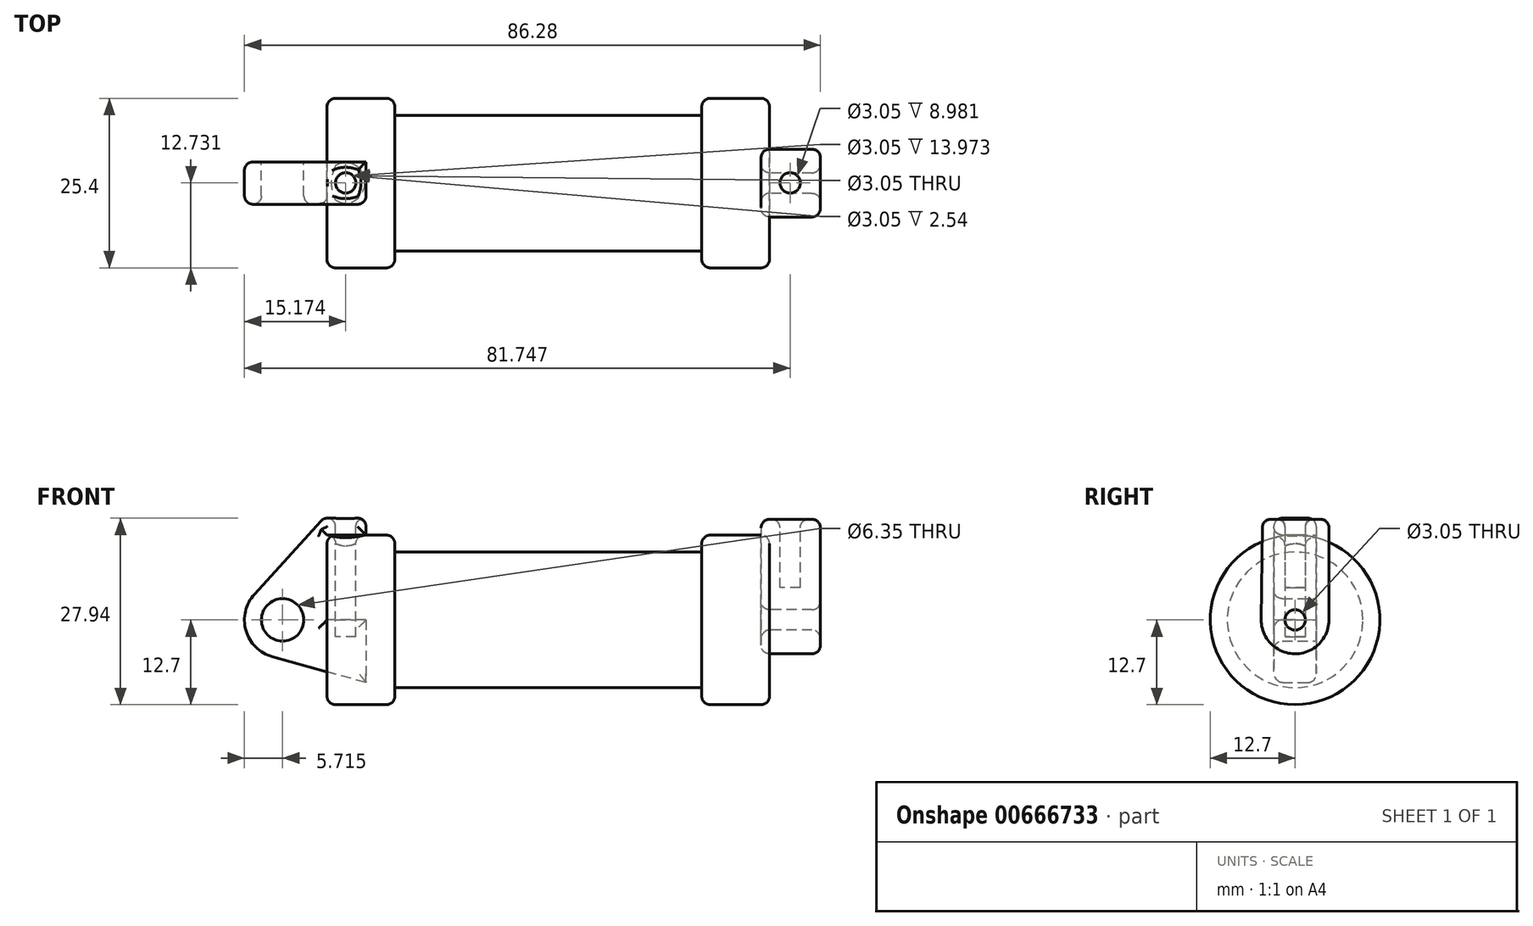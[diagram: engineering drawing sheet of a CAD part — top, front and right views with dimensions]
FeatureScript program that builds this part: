
annotation { "Feature Type Name" : "Feature", "Feature Type Description" : "" }
export const myFeature = defineFeature(function(context is Context, id is Id, definition is map)
    precondition{}
    {
        {
            var Q0;
            Q0=qCreatedBy(makeId("Front.planeOp"),FACE);
            var sketch = newSketch(context, id + "F0", { "sketchPlane" : qUnion([Q0])});
            skLineSegment(sketch, "E0", {"start": v(0, 0) * mm, "end": v(0, 12.7) * mm});
            skLineSegment(sketch, "E1", {"start": v(0, 12.7) * mm, "end": v(10.16, 12.7) * mm});
            skLineSegment(sketch, "E2", {"start": v(10.16, 12.7) * mm, "end": v(10.16, 10.16) * mm});
            skLineSegment(sketch, "E3", {"start": v(10.16, 10.16) * mm, "end": v(56.13, 10.16) * mm});
            skLineSegment(sketch, "E4", {"start": v(56.13, 10.16) * mm, "end": v(56.13, 12.7) * mm});
            skLineSegment(sketch, "E5", {"start": v(56.13, 12.7) * mm, "end": v(66.3, 12.7) * mm});
            skLineSegment(sketch, "E6", {"start": v(66.3, 12.7) * mm, "end": v(66.3, 0) * mm});
            skLineSegment(sketch, "E7", {"start": v(66.3, 0) * mm, "end": v(0, 0) * mm});
            skLineSegment(sketch, "E8", {"start": v(5.84, 15.24) * mm, "end": v(-0.5, 15.24) * mm});
            skLineSegment(sketch, "E9", {"start": v(-0.5, 15.24) * mm, "end": v(-10.88, 3.85) * mm});
            skLineSegment(sketch, "E10", {"start": v(0, 0) * mm, "end": v(-6.65, 0) * mm});
            skCircle(sketch, "E11", {"center": v(-6.65, 0) * mm, "radius": 5.72 * mm});
            skCircle(sketch, "E12", {"center": v(-6.65, 0) * mm, "radius": 3.18 * mm});
            skLineSegment(sketch, "E13", {"start": v(5.84, 15.24) * mm, "end": v(5.84, -9.4) * mm});
            skLineSegment(sketch, "E14", {"start": v(5.84, -9.4) * mm, "end": v(-8.18, -5.5) * mm});
            skSolve(sketch);
        }
        {
            var Q0;
            {var subQ1=sQuery(id+"F0.wireOp",EDGE,"E0");Q0=makeQuery(id+"F0.imprint","IMPRINT",FACE,{"disambiguationData":[TD([[makeQuery(id+"F0.imprint","IMPRINT",EDGE,{"derivedFrom":subQ1}),1.0]])]});}
            var Q1;
            {var subQ0=sQuery(id+"F0.wireOp",EDGE,"E14");Q1=makeQuery(id+"F0.imprint","IMPRINT",FACE,{"disambiguationData":[TD([[makeQuery(id+"F0.imprint","IMPRINT",EDGE,{"derivedFrom":subQ0}),-1.0]])]});}
            var Q2;
            {var subQ5=sQuery(id+"F0.wireOp",EDGE,"E12");Q2=makeQuery(id+"F0.imprint","IMPRINT",FACE,{"disambiguationData":[TD([[makeQuery(id+"F0.imprint","IMPRINT",EDGE,{"derivedFrom":subQ5}),-1.0]])]});}
            extrude(context, id + "F1", {"entities" : qUnion([Q0, Q1, Q2]), "endBound" : BoundingType.SYMMETRIC, "depth" : 6.35 * mm, "offsetDistance" : 25.4 * mm});
        }
        {
            var Q0;
            {var subQ0=sQuery(id+"F0.wireOp",EDGE,"E2");Q0=makeQuery(id+"F0.imprint","IMPRINT",FACE,{"disambiguationData":[TD([[makeQuery(id+"F0.imprint","IMPRINT",EDGE,{"derivedFrom":subQ0}),-1.0]])]});}
            var Q1;
            {var subQ0=sQuery(id+"F0.wireOp",EDGE,"E0");Q1=makeQuery(id+"F0.imprint","IMPRINT",FACE,{"disambiguationData":[TD([[makeQuery(id+"F0.imprint","IMPRINT",EDGE,{"derivedFrom":subQ0}),-1.0]])]});}
            var Q2;
            Q2=sQuery(id+"F0.wireOp",EDGE,"E7");
            revolve(context, id + "F2", {"entities" : qUnion([Q0, Q1]), "axis" : qUnion([Q2]), "revolveType" : RevolveType.FULL});
        }
        {
            var Q0;
            Q0=makeQuery(id+"F2.opRevolve","SWEPT_FACE",FACE,{"disambiguationData":[OSD([sQuery(id+"F0.wireOp",EDGE,"E6")])]});
            var sketch = newSketch(context, id + "F3", { "sketchPlane" : qUnion([Q0])});
            skCircle(sketch, "E15", {"center": v(0, 0) * mm, "radius": 1.52 * mm});
            skCircle(sketch, "E16", {"center": v(0, 0) * mm, "radius": 5.08 * mm});
            skLineSegment(sketch, "E17", {"start": v(5.08, 0) * mm, "end": v(5.08, 15.08) * mm});
            skLineSegment(sketch, "E18", {"start": v(5.08, 15.08) * mm, "end": v(-4.9, 15.08) * mm});
            skLineSegment(sketch, "E19", {"start": v(-4.9, 15.08) * mm, "end": v(-5.08, 0.03) * mm});
            skSolve(sketch);
        }
        {
            var Q0;
            Q0 = qSketchRegion(id + "F3", true);
            extrude(context, id + "F4", {"entities" : qUnion([Q0]), "depth" : 7.62 * mm, "offsetDistance" : 25.4 * mm, "hasSecondDirection" : true, "secondDirectionOppositeDirection" : true, "secondDirectionDepth" : 1.27 * mm});
        }
        {
            var Q0;
            Q0=makeQuery(id+"F2.opRevolve","SWEPT_FACE",FACE,{"disambiguationData":[OSD([sQuery(id+"F0.wireOp",EDGE,"E0")])]});
            var sketch = newSketch(context, id + "F5", { "sketchPlane" : qUnion([Q0])});
            skCircle(sketch, "E20", {"center": v(0, 0) * mm, "radius": 10.27 * mm});
            skSolve(sketch);
        }
        {
            var Q0;
            Q0=sQuery(id+"F5.wireOp",EDGE,"E20");
            extrude(context, id + "F6", {"bodyType" : ToolBodyType.SURFACE, "surfaceEntities" : qUnion([Q0]), "oppositeDirection" : true, "depth" : 63.5 * mm, "offsetDistance" : 25.4 * mm});
        }
        {
            var Q0;
            Q0=makeQuery(id+"F1.opExtrude","SWEPT_FACE",FACE,{"disambiguationData":[OSD([sQuery(id+"F0.wireOp",EDGE,"E8")])]});
            var sketch = newSketch(context, id + "F7", { "sketchPlane" : qUnion([Q0])});
            skCircle(sketch, "E21", {"center": v(2.8, 0.03) * mm, "radius": 1.52 * mm});
            skCircle(sketch, "E22", {"center": v(69.38, 0.03) * mm, "radius": 1.52 * mm});
            skSolve(sketch);
        }
        {
            var Q0;
            Q0=makeQuery(id+"F7.imprint","IMPRINT",FACE,{"disambiguationData":[TD([[makeQuery(id+"F7.imprint","IMPRINT",EDGE,{"derivedFrom":sQuery(id+"F7.wireOp",EDGE,"E21")}),1.0]])]});
            extrude(context, id + "F8", {"entities" : qUnion([Q0]), "operationType" : NewBodyOperationType.REMOVE, "oppositeDirection" : true, "depth" : 17.78 * mm, "offsetDistance" : 25.4 * mm});
        }
        {
            var Q0;
            Q0=makeQuery(id+"F7.imprint","IMPRINT",FACE,{"disambiguationData":[TD([[makeQuery(id+"F7.imprint","IMPRINT",EDGE,{"derivedFrom":sQuery(id+"F7.wireOp",EDGE,"E22")}),1.0]])]});
            extrude(context, id + "F9", {"entities" : qUnion([Q0]), "operationType" : NewBodyOperationType.REMOVE, "oppositeDirection" : true, "depth" : 10.4 * mm, "offsetDistance" : 25.4 * mm});
        }
        {
            var Q0;
            Q0=makeQuery(id+"F2.opRevolve","SWEPT_FACE",FACE,{"disambiguationData":[OSD([sQuery(id+"F0.wireOp",EDGE,"E1")])]});
            var Q1;
            Q1=makeQuery(id+"F6.opExtrude","SWEPT_FACE",FACE,{"disambiguationData":[OSD([sQuery(id+"F5.wireOp",EDGE,"E20")])]});
            var Q2;
            Q2=makeQuery(id+"F2.opRevolve","SWEPT_FACE",FACE,{"disambiguationData":[OSD([sQuery(id+"F0.wireOp",EDGE,"E5")])]});
            fillet(context, id + "F10", {"entities" : qUnion([Q0, Q1, Q2]), "radius" : 1.27 * mm, "tangentPropagation" : true, "allowEdgeOverflow" : false});
        }
        {
            var Q0;
            Q0=makeQuery(id+"F2.opRevolve","SWEPT_FACE",FACE,{"disambiguationData":[OSD([sQuery(id+"F0.wireOp",EDGE,"E6")])]});
            var Q1;
            Q1=makeQuery(id+"F1.opExtrude","SWEPT_FACE",FACE,{"disambiguationData":[OSD([sQuery(id+"F0.wireOp",EDGE,"E9")])]});
            var Q2;
            Q2=makeQuery(id+"F1.opExtrude","SWEPT_FACE",FACE,{"disambiguationData":[OSD([sQuery(id+"F0.wireOp",EDGE,"E8")])]});
            var Q3;
            Q3=makeQuery(id+"F1.opExtrude","SWEPT_FACE",FACE,{"disambiguationData":[OSD([sQuery(id+"F0.wireOp",EDGE,"E11")])]});
            var Q4;
            Q4=makeQuery(id+"F4.opExtrude","SWEPT_FACE",FACE,{"disambiguationData":[OSD([sQuery(id+"F3.wireOp",EDGE,"E18")])]});
            var Q5;
            Q5=makeQuery(id+"F9.opExtrude","CAP_EDGE",EDGE,{"disambiguationData":[OSD([sQuery(id+"F7.wireOp",EDGE,"E22")])],"isStart":false});
            var Q6;
            Q6=makeQuery(id+"F4.opExtrude","SWEPT_FACE",FACE,{"disambiguationData":[OSD([sQuery(id+"F3.wireOp",EDGE,"E17")])]});
            var Q7;
            Q7=makeQuery(id+"F4.opExtrude","SWEPT_FACE",FACE,{"disambiguationData":[OSD([sQuery(id+"F3.wireOp",EDGE,"E16")])]});
            var Q8;
            Q8=makeQuery(id+"F1.opExtrude","CAP_FACE",FACE,{"disambiguationData":[OSD([sQuery(id+"F0.wireOp",EDGE,"E0"),sQuery(id+"F0.wireOp",EDGE,"E1"),sQuery(id+"F0.wireOp",EDGE,"E7"),sQuery(id+"F0.wireOp",EDGE,"E8"),sQuery(id+"F0.wireOp",EDGE,"E9"),sQuery(id+"F0.wireOp",EDGE,"E11"),sQuery(id+"F0.wireOp",EDGE,"E12"),sQuery(id+"F0.wireOp",EDGE,"E13"),sQuery(id+"F0.wireOp",EDGE,"E14")])],"isStart":false});
            var Q9;
            Q9=makeQuery(id+"F8.opExtrude","CAP_EDGE",EDGE,{"disambiguationData":[OSD([sQuery(id+"F7.wireOp",EDGE,"E21")])],"isStart":true});
            var Q10;
            Q10=makeQuery(id+"F9.opExtrude","CAP_FACE",FACE,{"disambiguationData":[OSD([sQuery(id+"F7.wireOp",EDGE,"E22")])],"isStart":true});
            var Q11;
            Q11=makeQuery(id+"F4.opExtrude","CAP_EDGE",EDGE,{"disambiguationData":[OSD([sQuery(id+"F3.wireOp",EDGE,"E15")])],"isStart":false});
            var Q12;
            Q12=makeQuery(id+"F4.opExtrude","SWEPT_FACE",FACE,{"disambiguationData":[OSD([sQuery(id+"F3.wireOp",EDGE,"E19")])]});
            var Q13;
            Q13=makeQuery(id+"F4.opExtrude","CAP_EDGE",EDGE,{"disambiguationData":[OSD([sQuery(id+"F3.wireOp",EDGE,"E17")])],"isStart":false});
            var Q14;
            Q14=makeQuery(id+"F4.opExtrude","CAP_EDGE",EDGE,{"disambiguationData":[OSD([sQuery(id+"F3.wireOp",EDGE,"E16")])],"isStart":true});
            var Q15;
            Q15=makeQuery(id+"F4.opExtrude","SWEPT_EDGE",EDGE,{"disambiguationData":[OSD([sQuery(id+"F3.wireOp",EDGE,"E16"),sQuery(id+"F3.wireOp",EDGE,"E17")])]});
            var Q16;
            Q16=makeQuery(id+"F4.opExtrude","CAP_EDGE",EDGE,{"disambiguationData":[OSD([sQuery(id+"F3.wireOp",EDGE,"E19")])],"isStart":true});
            var Q17;
            Q17=makeQuery(id+"F4.opExtrude","SWEPT_EDGE",EDGE,{"disambiguationData":[OSD([sQuery(id+"F3.wireOp",EDGE,"E17"),sQuery(id+"F3.wireOp",EDGE,"E18")])]});
            var Q18;
            Q18=makeQuery(id+"F4.opExtrude","CAP_EDGE",EDGE,{"disambiguationData":[OSD([sQuery(id+"F3.wireOp",EDGE,"E17")])],"isStart":true});
            var Q19;
            Q19=makeQuery(id+"F4.opExtrude","CAP_EDGE",EDGE,{"disambiguationData":[OSD([sQuery(id+"F3.wireOp",EDGE,"E15")])],"isStart":true});
            var Q20;
            Q20=makeQuery(id+"F4.opExtrude","CAP_EDGE",EDGE,{"disambiguationData":[OSD([sQuery(id+"F3.wireOp",EDGE,"E18")])],"isStart":true});
            var Q21;
            Q21=makeQuery(id+"F9.opExtrude","CAP_EDGE",EDGE,{"disambiguationData":[OSD([sQuery(id+"F7.wireOp",EDGE,"E22")])],"isStart":true});
            fillet(context, id + "F11", {"entities" : qUnion([Q0, Q1, Q2, Q3, Q4, Q5, Q6, Q7, Q8, Q9, Q10, Q11, Q12, Q13, Q14, Q15, Q16, Q17, Q18, Q19, Q20, Q21]), "radius" : 1.27 * mm, "tangentPropagation" : true, "allowEdgeOverflow" : false});
        }
    });
